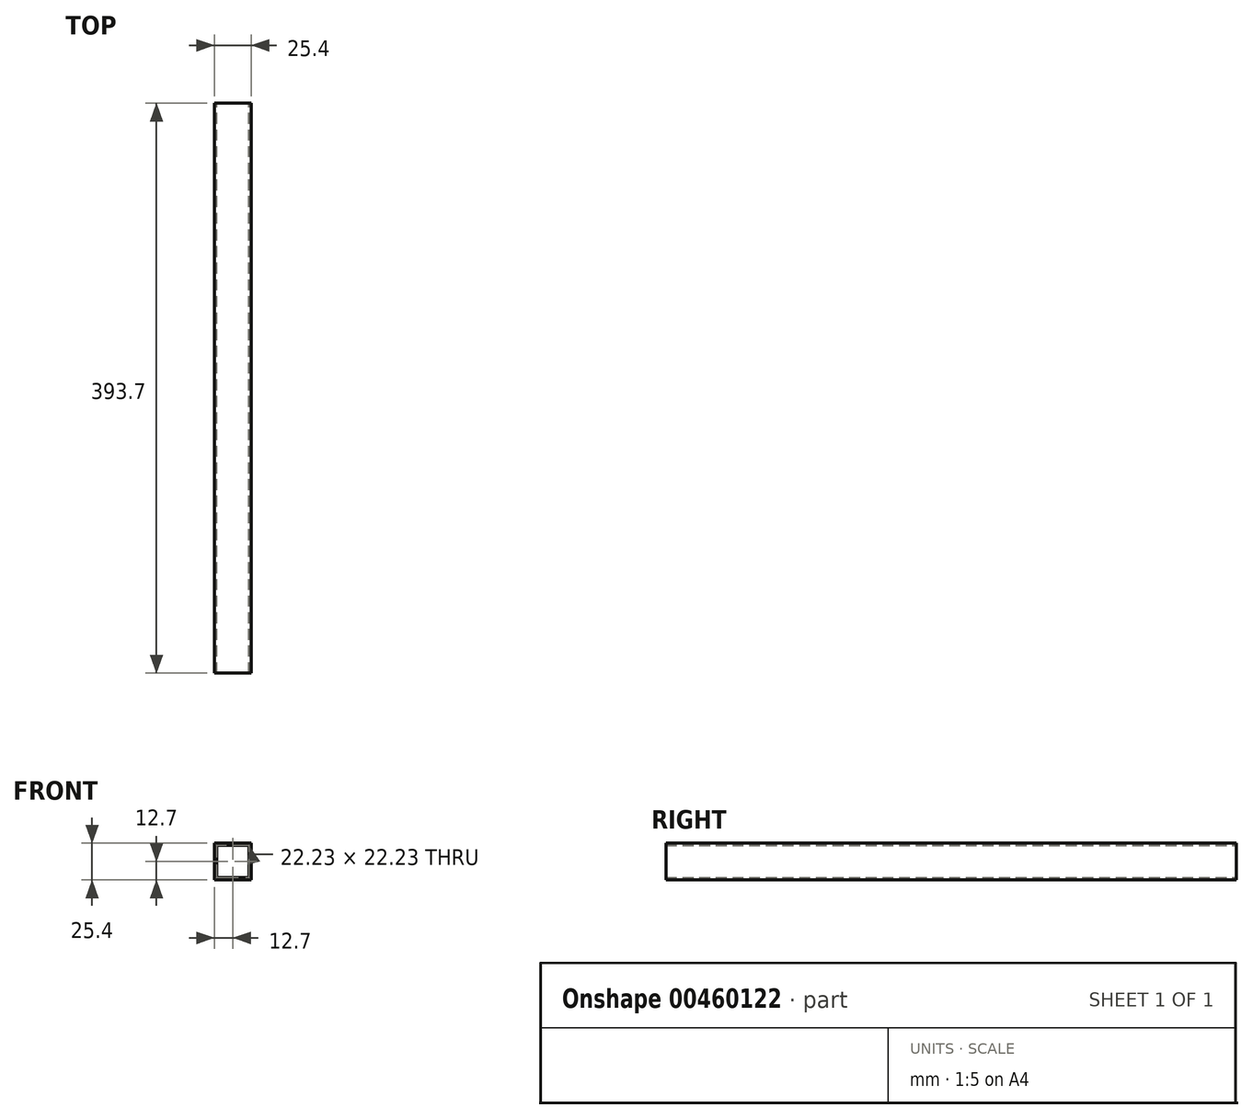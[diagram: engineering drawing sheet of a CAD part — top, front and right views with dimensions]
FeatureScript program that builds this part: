
annotation { "Feature Type Name" : "Feature", "Feature Type Description" : "" }
export const myFeature = defineFeature(function(context is Context, id is Id, definition is map)
    precondition{}
    {
        {
            var Q0;
            Q0=qCreatedBy(makeId("Front.planeOp"),FACE);
            var sketch = newSketch(context, id + "F0", { "sketchPlane" : qUnion([Q0])});
            skLineSegment(sketch, "E0.bottom", {"start": v(12.7, 12.7) * mm, "end": v(-12.7, 12.7) * mm});
            skLineSegment(sketch, "E0.top", {"start": v(12.7, -12.7) * mm, "end": v(-12.7, -12.7) * mm});
            skLineSegment(sketch, "E0.left", {"start": v(12.7, 12.7) * mm, "end": v(12.7, -12.7) * mm});
            skLineSegment(sketch, "E0.right", {"start": v(-12.7, 12.7) * mm, "end": v(-12.7, -12.7) * mm});
            skPoint(sketch, "E0.middle", {"position": v(0, 0) * mm});
            skLineSegment(sketch, "E1.bottom", {"start": v(11.11, 11.11) * mm, "end": v(-11.11, 11.11) * mm});
            skLineSegment(sketch, "E1.top", {"start": v(11.11, -11.11) * mm, "end": v(-11.11, -11.11) * mm});
            skLineSegment(sketch, "E1.left", {"start": v(11.11, 11.11) * mm, "end": v(11.11, -11.11) * mm});
            skLineSegment(sketch, "E1.right", {"start": v(-11.11, 11.11) * mm, "end": v(-11.11, -11.11) * mm});
            skSolve(sketch);
        }
        {
            var Q0;
            Q0=makeQuery(id+"F0.imprint","IMPRINT",FACE,{"disambiguationData":[TD([[makeQuery(id+"F0.imprint","IMPRINT",EDGE,{"derivedFrom":sQuery(id+"F0.wireOp",EDGE,"E0.bottom")}),1.0]])]});
            extrude(context, id + "F1", {"entities" : qUnion([Q0]), "depth" : 393.7 * mm});
        }
    });
